# Revit family: Toilet_TOTO_CST243EF
name_source: partatom
category: Plumbing Fixtures
revit_build: Autodesk Revit Architecture 2012 (Build: 20110916_2132(x64)
units: mm (PartAtom-declared; Revit-internal decimal feet)

## types (2) — shared parameters
ADA Compliant = No
Assembly Code = D2010110
CW Connection = Yes
Certifications = IAPMO (cUPC)
Code Compliance = UPC, IPC, NSPC, NPC Canada, and others
Cold Water Connection NPT Radius = 0' - 0 1/4"
Default Elevation = 0' - 0"
Description = Close Coupled Toilet
Flush System = E-Max
Gallons Per Flush = 1.3 gal
HW Connection = No
Handle Material = Polished Chrome
Height = 2' - 6"
Industry Standards = Meets and exceeds ASME A112.19.2/CSA B45.1
Installation URL = http://assets.totousa.com
Keynote = 22 42 13
Length = 2' - 2 5/8"
Manufacturer = TOTO USA, Inc.
Manufacturer Fax = (770) 282-0002
Model = CST243EF
Mount Type = Floor-Mounted
Parts Manual URL = http://assets.totousa.com
Product Page URL = http://www.totousa.com
Rough in Distance = 1' - 0"
Series = Entrada
Shipping Weight = 76.00 lb
Spec Sheet URL = http://assets.totousa.com
Style = Round Front
Supply Connection Height Offset = 0' - 8"
Supply Connection Offset from Center = 0' - 6"
URL = http://www.totousa.com
Vent Connection = Yes
Warranty = One Year Limited
Warranty Document = http://www.totousa.com
Waste Connection = Yes
Waste Connection Offset from Wall = 1' - 0"
WaterSense = Yes
Width = 1' - 2 3/8"
zero-valued in all types: CWFU, HWFU, WFU

## per-type parameters (varying)
| type | Fixture Material | Lid Material |
| #01 Cotton | Vitreous China - TOTO - 01 Cotton | Plastic - Cotton |
| #12 Sedona Beige | Vitreous China - TOTO - 12 Sedona Beige | Plastic - Beige |

## geometry (parser evidence)
native form markers: Blend x16, Sweep x1
no freeform markers — native parametric forms only
